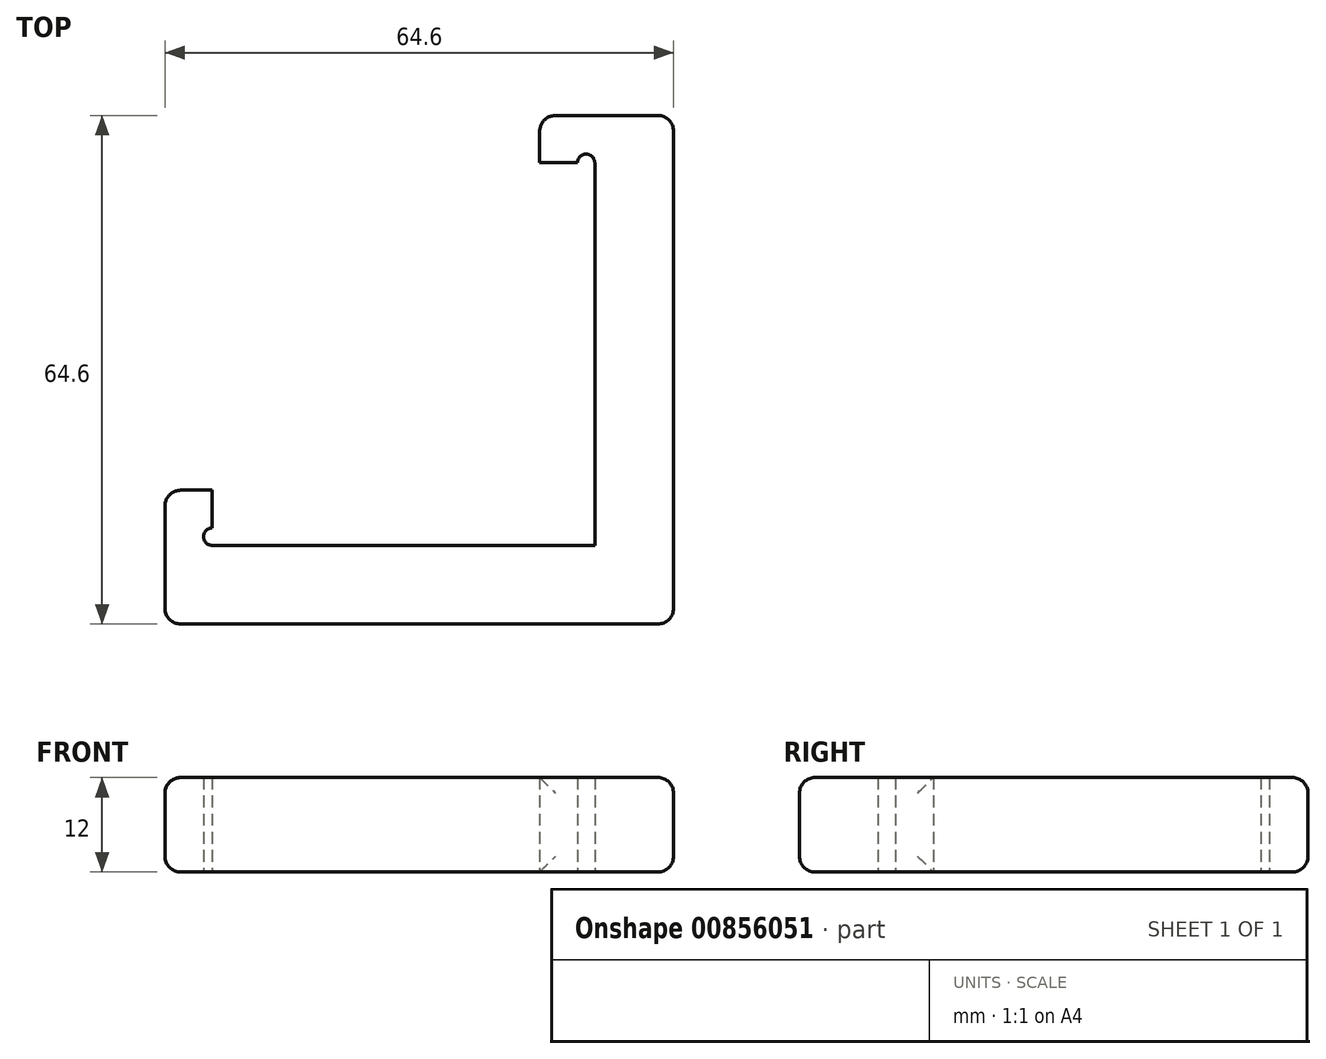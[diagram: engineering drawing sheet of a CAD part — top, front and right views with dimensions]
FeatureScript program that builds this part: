
annotation { "Feature Type Name" : "Feature", "Feature Type Description" : "" }
export const myFeature = defineFeature(function(context is Context, id is Id, definition is map)
    precondition{}
    {
        {
            var Q0;
            Q0=qCreatedBy(makeId("Top.planeOp"),FACE);
            var sketch = newSketch(context, id + "F0", { "sketchPlane" : qUnion([Q0])});
            skLineSegment(sketch, "E0.bottom", {"start": v(0, 0) * mm, "end": v(64.6, 0) * mm});
            skLineSegment(sketch, "E0.top", {"start": v(0, 17) * mm, "end": v(6, 17) * mm});
            skLineSegment(sketch, "E0.left", {"start": v(0, 0) * mm, "end": v(0, 17) * mm});
            skLineSegment(sketch, "E0.right", {"start": v(64.6, 0) * mm, "end": v(64.6, 64.6) * mm});
            skLineSegment(sketch, "E1.top", {"start": v(6, 10) * mm, "end": v(54.6, 10) * mm});
            skLineSegment(sketch, "E1.left", {"start": v(6, 17) * mm, "end": v(6, 10) * mm});
            skLineSegment(sketch, "E1.right", {"start": v(54.6, 58.6) * mm, "end": v(54.6, 10) * mm});
            skLineSegment(sketch, "E2.bottom", {"start": v(64.6, 64.6) * mm, "end": v(47.6, 64.6) * mm});
            skLineSegment(sketch, "E2.top", {"start": v(54.6, 58.6) * mm, "end": v(47.6, 58.6) * mm});
            skLineSegment(sketch, "E2.left", {"start": v(64.6, 64.6) * mm, "end": v(64.6, 58.6) * mm});
            skLineSegment(sketch, "E2.right", {"start": v(47.6, 64.6) * mm, "end": v(47.6, 58.6) * mm});
            skSolve(sketch);
        }
        {
            var Q0;
            Q0 = qSketchRegion(id + "F0", true);
            extrude(context, id + "F1", {"entities" : qUnion([Q0]), "depth" : 12 * mm, "offsetDistance" : 25 * mm});
        }
        {
            var Q0;
            Q0=qCreatedBy(makeId("Top.planeOp"),FACE);
            var sketch = newSketch(context, id + "F2", { "sketchPlane" : qUnion([Q0])});
            skCircle(sketch, "E3", {"center": v(6, 11.1) * mm, "radius": 1.1 * mm});
            skCircle(sketch, "E4", {"center": v(53.5, 58.6) * mm, "radius": 1.1 * mm});
            skSolve(sketch);
        }
        {
            var Q0;
            Q0 = qSketchRegion(id + "F2", true);
            extrude(context, id + "F3", {"entities" : qUnion([Q0]), "operationType" : NewBodyOperationType.REMOVE, "endBound" : BoundingType.THROUGH_ALL, "depth" : 25 * mm, "offsetDistance" : 25 * mm});
        }
        {
            var Q0;
            Q0=makeQuery(id+"F1.opExtrude","SWEPT_FACE",FACE,{"disambiguationData":[OSD([sQuery(id+"F0.wireOp",EDGE,"E0.bottom")])]});
            var Q1;
            Q1=makeQuery(id+"F1.opExtrude","SWEPT_FACE",FACE,{"disambiguationData":[OSD([sQuery(id+"F0.wireOp",EDGE,"E0.left")])]});
            var Q2;
            Q2=makeQuery(id+"F1.opExtrude","SWEPT_FACE",FACE,{"disambiguationData":[OSD([sQuery(id+"F0.wireOp",EDGE,"E0.right")])]});
            var Q3;
            Q3=makeQuery(id+"F1.opExtrude","SWEPT_FACE",FACE,{"disambiguationData":[OSD([sQuery(id+"F0.wireOp",EDGE,"E2.bottom")])]});
            fillet(context, id + "F4", {"entities" : qUnion([Q0, Q1, Q2, Q3]), "radius" : 2 * mm, "tangentPropagation" : true, "allowEdgeOverflow" : false});
        }
    });
